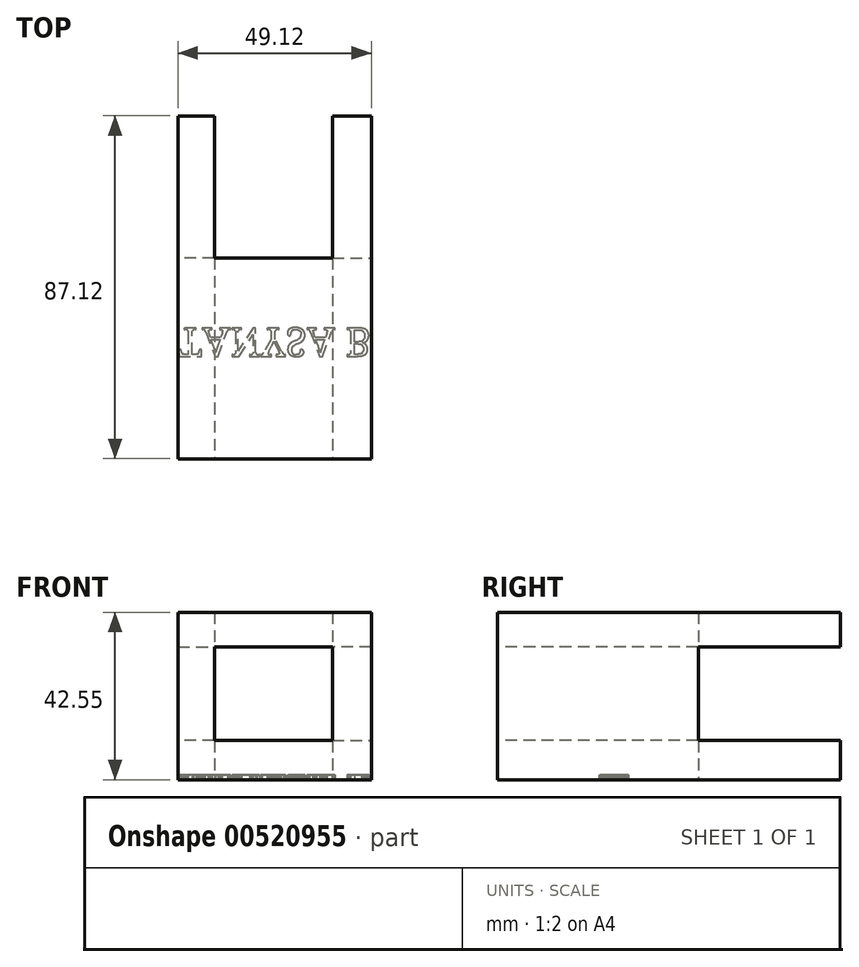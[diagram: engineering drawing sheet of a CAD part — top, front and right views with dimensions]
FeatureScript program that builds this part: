
annotation { "Feature Type Name" : "Feature", "Feature Type Description" : "" }
export const myFeature = defineFeature(function(context is Context, id is Id, definition is map)
    precondition{}
    {
        {
            var Q0;
            Q0=qCreatedBy(makeId("Front.planeOp"),FACE);
            var sketch = newSketch(context, id + "F0", { "sketchPlane" : qUnion([Q0])});
            skLineSegment(sketch, "E0.bottom", {"start": v(0, 0) * mm, "end": v(-49.12, 0) * mm});
            skLineSegment(sketch, "E0.top", {"start": v(0, 42.55) * mm, "end": v(-49.12, 42.55) * mm});
            skLineSegment(sketch, "E0.left", {"start": v(0, 0) * mm, "end": v(0, 42.55) * mm});
            skLineSegment(sketch, "E0.right", {"start": v(-49.12, 0) * mm, "end": v(-49.12, 42.55) * mm});
            skSolve(sketch);
        }
        {
            var Q0;
            Q0=makeQuery(id+"F0.imprint","IMPRINT",FACE,{"disambiguationData":[TD([[makeQuery(id+"F0.imprint","IMPRINT",EDGE,{"derivedFrom":sQuery(id+"F0.wireOp",EDGE,"E0.bottom")}),-1.0]])]});
            extrude(context, id + "F1", {"entities" : qUnion([Q0]), "depth" : 51.05 * mm, "offsetDistance" : 25.4 * mm});
        }
        {
            var Q0;
            Q0=makeQuery(id+"F1.opExtrude","CAP_FACE",FACE,{"disambiguationData":[OSD([sQuery(id+"F0.wireOp",EDGE,"E0.bottom"),sQuery(id+"F0.wireOp",EDGE,"E0.top"),sQuery(id+"F0.wireOp",EDGE,"E0.left"),sQuery(id+"F0.wireOp",EDGE,"E0.right")])],"isStart":false});
            var sketch = newSketch(context, id + "F2", { "sketchPlane" : qUnion([Q0])});
            skLineSegment(sketch, "E1.bottom", {"start": v(-39.89, 33.68) * mm, "end": v(-9.92, 33.68) * mm});
            skLineSegment(sketch, "E1.top", {"start": v(-39.89, 9.96) * mm, "end": v(-9.92, 9.96) * mm});
            skLineSegment(sketch, "E1.left", {"start": v(-39.89, 33.68) * mm, "end": v(-39.89, 9.96) * mm});
            skLineSegment(sketch, "E1.right", {"start": v(-9.92, 33.68) * mm, "end": v(-9.92, 9.96) * mm});
            skSolve(sketch);
        }
        {
            var Q0;
            Q0=makeQuery(id+"F2.imprint","IMPRINT",FACE,{"disambiguationData":[TD([[makeQuery(id+"F2.imprint","IMPRINT",EDGE,{"derivedFrom":sQuery(id+"F2.wireOp",EDGE,"E1.bottom")}),-1.0]])]});
            extrude(context, id + "F3", {"entities" : qUnion([Q0]), "operationType" : NewBodyOperationType.REMOVE, "oppositeDirection" : true, "depth" : 62.23 * mm, "offsetDistance" : 25.4 * mm});
        }
        {
            var Q0;
            Q0=makeQuery(id+"F1.opExtrude","CAP_FACE",FACE,{"disambiguationData":[OSD([sQuery(id+"F0.wireOp",EDGE,"E0.bottom"),sQuery(id+"F0.wireOp",EDGE,"E0.top"),sQuery(id+"F0.wireOp",EDGE,"E0.left"),sQuery(id+"F0.wireOp",EDGE,"E0.right")])],"isStart":true});
            var sketch = newSketch(context, id + "F4", { "sketchPlane" : qUnion([Q0])});
            skLineSegment(sketch, "E2.bottom", {"start": v(0, 42.55) * mm, "end": v(9.92, 42.55) * mm});
            skLineSegment(sketch, "E2.top", {"start": v(0, 33.68) * mm, "end": v(9.92, 33.68) * mm});
            skLineSegment(sketch, "E2.left", {"start": v(0, 42.55) * mm, "end": v(0, 33.68) * mm});
            skLineSegment(sketch, "E2.right", {"start": v(9.92, 42.55) * mm, "end": v(9.92, 33.68) * mm});
            skLineSegment(sketch, "E3.bottom", {"start": v(49.12, 42.55) * mm, "end": v(39.89, 42.55) * mm});
            skLineSegment(sketch, "E3.top", {"start": v(49.12, 33.68) * mm, "end": v(39.89, 33.68) * mm});
            skLineSegment(sketch, "E3.left", {"start": v(49.12, 42.55) * mm, "end": v(49.12, 33.68) * mm});
            skLineSegment(sketch, "E3.right", {"start": v(39.89, 42.55) * mm, "end": v(39.89, 33.68) * mm});
            skLineSegment(sketch, "E4.bottom", {"start": v(9.92, 9.96) * mm, "end": v(0, 9.96) * mm});
            skLineSegment(sketch, "E4.top", {"start": v(9.92, 0) * mm, "end": v(0, 0) * mm});
            skLineSegment(sketch, "E4.left", {"start": v(9.92, 9.96) * mm, "end": v(9.92, 0) * mm});
            skLineSegment(sketch, "E4.right", {"start": v(0, 9.96) * mm, "end": v(0, 0) * mm});
            skLineSegment(sketch, "E5.bottom", {"start": v(39.89, 9.96) * mm, "end": v(49.12, 9.96) * mm});
            skLineSegment(sketch, "E5.top", {"start": v(39.89, 0) * mm, "end": v(49.12, 0) * mm});
            skLineSegment(sketch, "E5.left", {"start": v(39.89, 9.96) * mm, "end": v(39.89, 0) * mm});
            skLineSegment(sketch, "E5.right", {"start": v(49.12, 9.96) * mm, "end": v(49.12, 0) * mm});
            skSolve(sketch);
        }
        {
            var Q0;
            Q0=makeQuery(id+"F4.imprint","IMPRINT",FACE,{"disambiguationData":[TD([[makeQuery(id+"F4.imprint","IMPRINT",EDGE,{"derivedFrom":sQuery(id+"F4.wireOp",EDGE,"E2.bottom")}),-1.0]])]});
            var Q1;
            Q1=makeQuery(id+"F4.imprint","IMPRINT",FACE,{"disambiguationData":[TD([[makeQuery(id+"F4.imprint","IMPRINT",EDGE,{"derivedFrom":sQuery(id+"F4.wireOp",EDGE,"E3.bottom")}),-1.0]])]});
            var Q2;
            Q2=makeQuery(id+"F4.imprint","IMPRINT",FACE,{"disambiguationData":[TD([[makeQuery(id+"F4.imprint","IMPRINT",EDGE,{"derivedFrom":sQuery(id+"F4.wireOp",EDGE,"E5.bottom")}),-1.0]])]});
            var Q3;
            Q3=makeQuery(id+"F4.imprint","IMPRINT",FACE,{"disambiguationData":[TD([[makeQuery(id+"F4.imprint","IMPRINT",EDGE,{"derivedFrom":sQuery(id+"F4.wireOp",EDGE,"E4.bottom")}),1.0]])]});
            extrude(context, id + "F5", {"entities" : qUnion([Q0, Q1, Q2, Q3]), "operationType" : NewBodyOperationType.ADD, "depth" : 36.07 * mm, "offsetDistance" : 25.4 * mm});
        }
        {
            var Q0;
            Q0=makeQuery(id+"F5.boolean.opBoolean","MERGE",FACE,{"derivedFrom":[makeQuery(id+"F1.opExtrude","SWEPT_FACE",FACE,{"disambiguationData":[OSD([sQuery(id+"F0.wireOp",EDGE,"E0.bottom")])]}),makeQuery(id+"F5.opExtrude","SWEPT_FACE",FACE,{"disambiguationData":[OSD([sQuery(id+"F4.wireOp",EDGE,"E4.top")])]}),makeQuery(id+"F5.opExtrude","SWEPT_FACE",FACE,{"disambiguationData":[OSD([sQuery(id+"F4.wireOp",EDGE,"E5.top")])]})]});
            var sketch = newSketch(context, id + "F6", { "sketchPlane" : qUnion([Q0])});
            skText(sketch, "E6", { "text": "TANYSA B", "fontName": "NotoSerif-Regular.ttf"});
            const initialGuessF6  = {"E6": [-0.04912, 0.01782, 1, 0, 0.00726]};
            skSetInitialGuess(sketch, initialGuessF6);
            skSolve(sketch);
        }
        {
            var Q0;
            Q0 = qSketchRegion(id + "F6", true);
            extrude(context, id + "F7", {"entities" : qUnion([Q0]), "operationType" : NewBodyOperationType.REMOVE, "oppositeDirection" : true, "depth" : 1.27 * mm, "offsetDistance" : 25.4 * mm});
        }
    });
